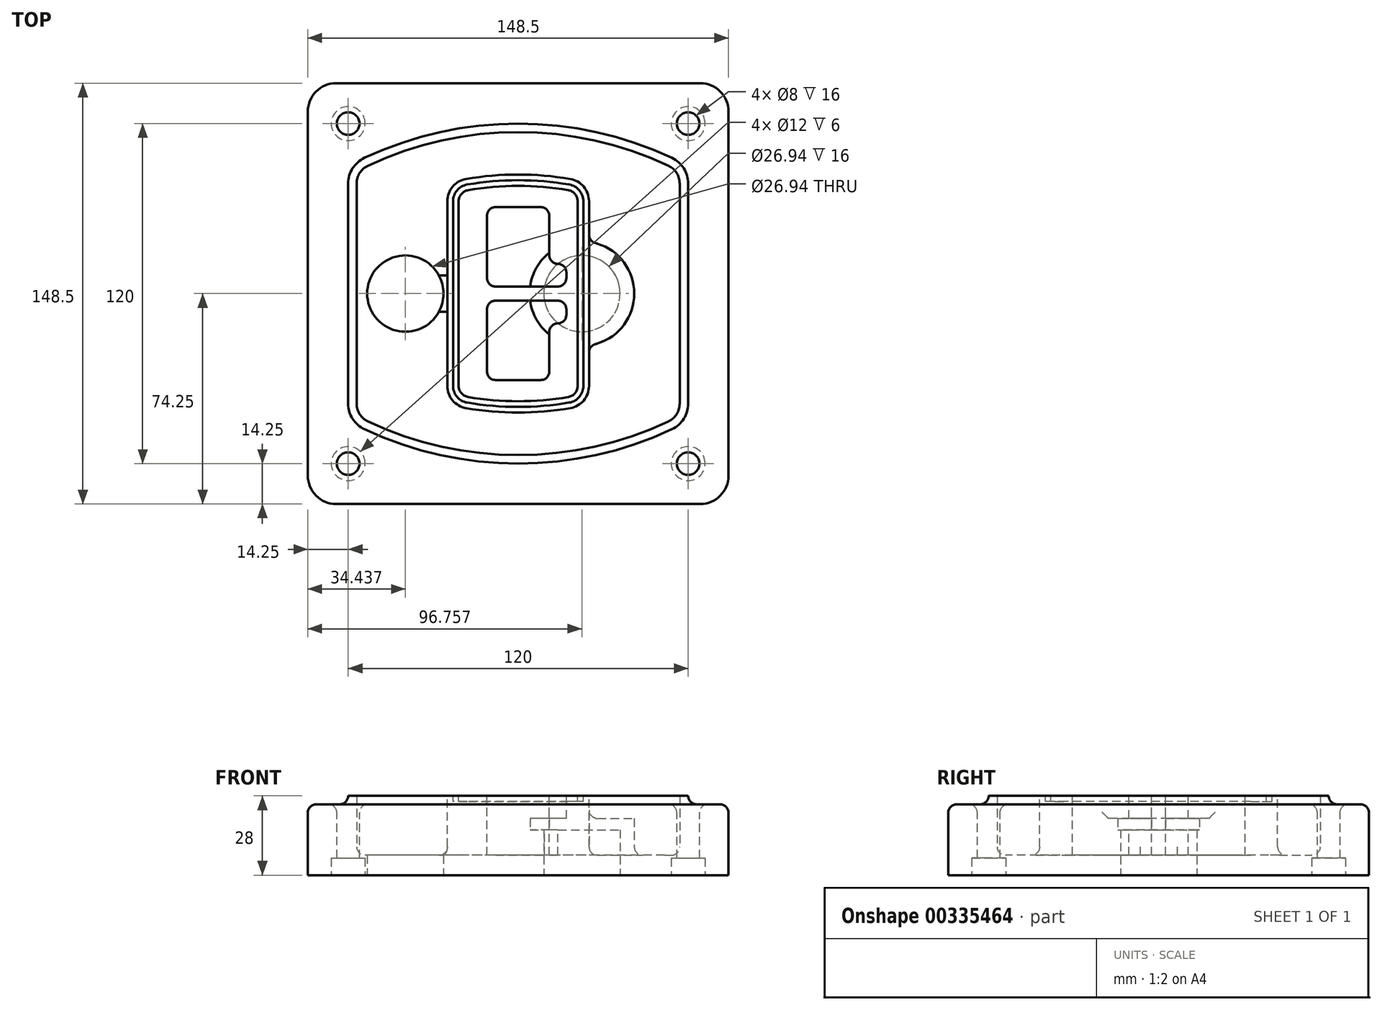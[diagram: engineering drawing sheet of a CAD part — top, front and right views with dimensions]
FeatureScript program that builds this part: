
annotation { "Feature Type Name" : "Feature", "Feature Type Description" : "" }
export const myFeature = defineFeature(function(context is Context, id is Id, definition is map)
    precondition{}
    {
        {
            var Q0;
            Q0=qCreatedBy(makeId("Top.planeOp"),FACE);
            var sketch = newSketch(context, id + "F0", { "sketchPlane" : qUnion([Q0])});
            skPoint(sketch, "E0.rect.middle", {"position": v(0, 0) * mm});
            skLineSegment(sketch, "E1.bottom", {"start": v(-64.25, -74.25) * mm, "end": v(64.25, -74.25) * mm});
            skLineSegment(sketch, "E1.top", {"start": v(-64.25, 74.25) * mm, "end": v(64.25, 74.25) * mm});
            skLineSegment(sketch, "E1.left", {"start": v(-74.25, -64.25) * mm, "end": v(-74.25, 64.25) * mm});
            skLineSegment(sketch, "E1.right", {"start": v(74.25, -64.25) * mm, "end": v(74.25, 64.25) * mm});
            skLineSegment(sketch, "E2", {"start": v(-74.25, 74.25) * mm, "end": v(74.25, -74.25) * mm, "construction": true});
            skLineSegment(sketch, "E3", {"start": v(74.25, 74.25) * mm, "end": v(-74.25, -74.25) * mm, "construction": true});
            skCircle(sketch, "E4", {"center": v(-60, 60) * mm, "radius": 4 * mm});
            skCircle(sketch, "E5", {"center": v(60, 60) * mm, "radius": 4 * mm});
            skCircle(sketch, "E6", {"center": v(60, -60) * mm, "radius": 4 * mm});
            skCircle(sketch, "E7", {"center": v(-60, -60) * mm, "radius": 4 * mm});
            skLineSegment(sketch, "E8", {"start": v(-60, 60) * mm, "end": v(60, 60) * mm, "construction": true});
            skLineSegment(sketch, "E9", {"start": v(60, 60) * mm, "end": v(60, -60) * mm, "construction": true});
            skLineSegment(sketch, "E10", {"start": v(60, -60) * mm, "end": v(-60, -60) * mm, "construction": true});
            skLineSegment(sketch, "E11", {"start": v(-60, -60) * mm, "end": v(-60, 60) * mm, "construction": true});
            skLineSegment(sketch, "E12", {"start": v(-60, 38.83) * mm, "end": v(-60, -38.83) * mm});
            skLineSegment(sketch, "E13", {"start": v(60, 38.83) * mm, "end": v(60, -38.83) * mm});
            skArc(sketch, "E14", {"start": v(54.26, 47.88) * mm, "mid": v(0, 60) * mm, "end": v(-54.26, 47.88) * mm});
            skArc(sketch, "E15", {"start": v(-54.26, -47.88) * mm, "mid": v(0, -60) * mm, "end": v(54.26, -47.88) * mm});
            skLineSegment(sketch, "E16", {"start": v(-60, 0) * mm, "end": v(60, 0) * mm, "construction": true});
            skPoint(sketch, "E17.visualSharp", {"position": v(-60, -45) * mm});
            skArc(sketch, "E17.filletArc", {"start": v(-60, -38.83) * mm, "mid": v(-58.44, -44.2) * mm, "end": v(-54.26, -47.88) * mm});
            skPoint(sketch, "E18.visualSharp", {"position": v(-60, 45) * mm});
            skArc(sketch, "E18.filletArc", {"start": v(-54.26, 47.88) * mm, "mid": v(-58.44, 44.2) * mm, "end": v(-60, 38.83) * mm});
            skPoint(sketch, "E19.visualSharp", {"position": v(60, 45) * mm});
            skArc(sketch, "E19.filletArc", {"start": v(60, 38.83) * mm, "mid": v(58.44, 44.2) * mm, "end": v(54.26, 47.88) * mm});
            skPoint(sketch, "E20.visualSharp", {"position": v(60, -45) * mm});
            skArc(sketch, "E20.filletArc", {"start": v(54.26, -47.88) * mm, "mid": v(58.44, -44.2) * mm, "end": v(60, -38.83) * mm});
            skPoint(sketch, "E21.visualSharp", {"position": v(-74.25, 74.25) * mm});
            skArc(sketch, "E21.filletArc", {"start": v(-64.25, 74.25) * mm, "mid": v(-71.32, 71.32) * mm, "end": v(-74.25, 64.25) * mm});
            skPoint(sketch, "E22.visualSharp", {"position": v(74.25, 74.25) * mm});
            skArc(sketch, "E22.filletArc", {"start": v(74.25, 64.25) * mm, "mid": v(71.32, 71.32) * mm, "end": v(64.25, 74.25) * mm});
            skPoint(sketch, "E23.visualSharp", {"position": v(74.25, -74.25) * mm});
            skArc(sketch, "E23.filletArc", {"start": v(64.25, -74.25) * mm, "mid": v(71.32, -71.32) * mm, "end": v(74.25, -64.25) * mm});
            skPoint(sketch, "E24.visualSharp", {"position": v(-74.25, -74.25) * mm});
            skArc(sketch, "E24.filletArc", {"start": v(-74.25, -64.25) * mm, "mid": v(-71.32, -71.32) * mm, "end": v(-64.25, -74.25) * mm});
            skArc(sketch, "E25.0", {"start": v(57, 38.83) * mm, "mid": v(55.9, 42.58) * mm, "end": v(52.98, 45.17) * mm});
            skLineSegment(sketch, "E25.1", {"start": v(57, 38.83) * mm, "end": v(57, -38.83) * mm});
            skArc(sketch, "E25.2", {"start": v(52.98, -45.17) * mm, "mid": v(55.9, -42.58) * mm, "end": v(57, -38.83) * mm});
            skArc(sketch, "E25.3", {"start": v(-52.98, -45.17) * mm, "mid": v(0, -57) * mm, "end": v(52.98, -45.17) * mm});
            skArc(sketch, "E25.4", {"start": v(-57, -38.83) * mm, "mid": v(-55.9, -42.58) * mm, "end": v(-52.98, -45.17) * mm});
            skArc(sketch, "E25.5", {"start": v(52.98, 45.17) * mm, "mid": v(0, 57) * mm, "end": v(-52.98, 45.17) * mm});
            skLineSegment(sketch, "E25.6", {"start": v(-57, 38.83) * mm, "end": v(-57, -38.83) * mm});
            skArc(sketch, "E25.7", {"start": v(-52.98, 45.17) * mm, "mid": v(-55.9, 42.58) * mm, "end": v(-57, 38.83) * mm});
            skArc(sketch, "E26.0", {"start": v(-55.96, 51.5) * mm, "mid": v(-61.82, 46.33) * mm, "end": v(-64, 38.83) * mm});
            skArc(sketch, "E26.1", {"start": v(55.96, 51.5) * mm, "mid": v(0, 64) * mm, "end": v(-55.96, 51.5) * mm});
            skArc(sketch, "E26.2", {"start": v(64, 38.83) * mm, "mid": v(61.82, 46.33) * mm, "end": v(55.96, 51.5) * mm});
            skLineSegment(sketch, "E26.3", {"start": v(64, 38.83) * mm, "end": v(64, -38.83) * mm});
            skArc(sketch, "E26.4", {"start": v(55.96, -51.5) * mm, "mid": v(61.82, -46.33) * mm, "end": v(64, -38.83) * mm});
            skLineSegment(sketch, "E26.5", {"start": v(-64, 38.83) * mm, "end": v(-64, -38.83) * mm});
            skArc(sketch, "E26.6", {"start": v(-55.96, -51.5) * mm, "mid": v(0, -64) * mm, "end": v(55.96, -51.5) * mm});
            skArc(sketch, "E26.7", {"start": v(-64, -38.83) * mm, "mid": v(-61.82, -46.33) * mm, "end": v(-55.96, -51.5) * mm});
            skSolve(sketch);
        }
        {
            var Q0;
            Q0=makeQuery(id+"F0.imprint","IMPRINT",FACE,{"disambiguationData":[TD([[makeQuery(id+"F0.imprint","IMPRINT",EDGE,{"derivedFrom":sQuery(id+"F0.wireOp",EDGE,"E1.bottom")}),1.0]])]});
            var Q1;
            Q1=makeQuery(id+"F0.imprint","IMPRINT",FACE,{"disambiguationData":[TD([[makeQuery(id+"F0.imprint","IMPRINT",EDGE,{"derivedFrom":sQuery(id+"F0.wireOp",EDGE,"E12")}),1.0]])]});
            var Q2;
            Q2=makeQuery(id+"F0.imprint","IMPRINT",FACE,{"disambiguationData":[TD([[makeQuery(id+"F0.imprint","IMPRINT",EDGE,{"derivedFrom":sQuery(id+"F0.wireOp",EDGE,"E25.0")}),1.0]])]});
            var Q3;
            Q3=makeQuery(id+"F0.imprint","IMPRINT",FACE,{"disambiguationData":[TD([[makeQuery(id+"F0.imprint","IMPRINT",EDGE,{"derivedFrom":sQuery(id+"F0.wireOp",EDGE,"E12")}),-1.0]])]});
            extrude(context, id + "F1", {"entities" : qUnion([Q0, Q1, Q2, Q3]), "oppositeDirection" : true, "depth" : 25 * mm});
        }
        {
            var Q0;
            Q0=makeQuery(id+"F0.imprint","IMPRINT",FACE,{"disambiguationData":[TD([[makeQuery(id+"F0.imprint","IMPRINT",EDGE,{"derivedFrom":sQuery(id+"F0.wireOp",EDGE,"E12")}),1.0]])]});
            extrude(context, id + "F2", {"entities" : qUnion([Q0]), "operationType" : NewBodyOperationType.ADD, "depth" : 3 * mm});
        }
        {
            var Q0;
            Q0=makeQuery(id+"F0.imprint","IMPRINT",FACE,{"disambiguationData":[TD([[makeQuery(id+"F0.imprint","IMPRINT",EDGE,{"derivedFrom":sQuery(id+"F0.wireOp",EDGE,"E25.0")}),1.0]])]});
            extrude(context, id + "F3", {"entities" : qUnion([Q0]), "operationType" : NewBodyOperationType.REMOVE, "oppositeDirection" : true, "depth" : 18 * mm});
        }
        {
            var Q0;
            Q0=makeQuery(id+"F2.opExtrude","CAP_FACE",FACE,{"disambiguationData":[OSD([sQuery(id+"F0.wireOp",EDGE,"E12"),sQuery(id+"F0.wireOp",EDGE,"E13"),sQuery(id+"F0.wireOp",EDGE,"E14"),sQuery(id+"F0.wireOp",EDGE,"E15"),sQuery(id+"F0.wireOp",EDGE,"E17.filletArc"),sQuery(id+"F0.wireOp",EDGE,"E18.filletArc"),sQuery(id+"F0.wireOp",EDGE,"E19.filletArc"),sQuery(id+"F0.wireOp",EDGE,"E20.filletArc"),sQuery(id+"F0.wireOp",EDGE,"E25.0"),sQuery(id+"F0.wireOp",EDGE,"E25.1"),sQuery(id+"F0.wireOp",EDGE,"E25.2"),sQuery(id+"F0.wireOp",EDGE,"E25.3"),sQuery(id+"F0.wireOp",EDGE,"E25.4"),sQuery(id+"F0.wireOp",EDGE,"E25.5"),sQuery(id+"F0.wireOp",EDGE,"E25.6"),sQuery(id+"F0.wireOp",EDGE,"E25.7")])],"isStart":false});
            var sketch = newSketch(context, id + "F4", { "sketchPlane" : qUnion([Q0])});
            skArc(sketch, "E27.0", {"start": v(-18.34, -40.45) * mm, "mid": v(0, -42) * mm, "end": v(18.34, -40.45) * mm});
            skArc(sketch, "E28.0", {"start": v(18.34, 40.45) * mm, "mid": v(0, 42) * mm, "end": v(-18.34, 40.45) * mm});
            skLineSegment(sketch, "E29", {"start": v(-25, 32.57) * mm, "end": v(-25, -32.57) * mm});
            skLineSegment(sketch, "E30", {"start": v(25, 32.57) * mm, "end": v(25, -32.57) * mm});
            skLineSegment(sketch, "E31", {"start": v(-25, 39.1) * mm, "end": v(25, 39.1) * mm, "construction": true});
            skLineSegment(sketch, "E32", {"start": v(-25, -39.1) * mm, "end": v(25, -39.1) * mm, "construction": true});
            skPoint(sketch, "E33.visualSharp", {"position": v(-25, 39.1) * mm});
            skArc(sketch, "E33.filletArc", {"start": v(-18.34, 40.45) * mm, "mid": v(-23.11, 37.73) * mm, "end": v(-25, 32.57) * mm});
            skPoint(sketch, "E34.visualSharp", {"position": v(25, 39.1) * mm});
            skArc(sketch, "E34.filletArc", {"start": v(25, 32.57) * mm, "mid": v(23.11, 37.73) * mm, "end": v(18.34, 40.45) * mm});
            skPoint(sketch, "E35.visualSharp", {"position": v(25, -39.1) * mm});
            skArc(sketch, "E35.filletArc", {"start": v(18.34, -40.45) * mm, "mid": v(23.11, -37.73) * mm, "end": v(25, -32.57) * mm});
            skPoint(sketch, "E36.visualSharp", {"position": v(-25, -39.1) * mm});
            skArc(sketch, "E36.filletArc", {"start": v(-25, -32.57) * mm, "mid": v(-23.11, -37.73) * mm, "end": v(-18.34, -40.45) * mm});
            skArc(sketch, "E37.0", {"start": v(52.98, 45.17) * mm, "mid": v(0, 57) * mm, "end": v(-52.98, 45.17) * mm});
            skArc(sketch, "E37.1", {"start": v(-52.98, 45.17) * mm, "mid": v(-55.9, 42.58) * mm, "end": v(-57, 38.83) * mm});
            skLineSegment(sketch, "E37.2", {"start": v(-57, 38.83) * mm, "end": v(-57, -38.83) * mm});
            skArc(sketch, "E37.3", {"start": v(-57, -38.83) * mm, "mid": v(-55.9, -42.58) * mm, "end": v(-52.98, -45.17) * mm});
            skArc(sketch, "E37.4", {"start": v(-52.98, -45.17) * mm, "mid": v(0, -57) * mm, "end": v(52.98, -45.17) * mm});
            skArc(sketch, "E37.5", {"start": v(52.98, -45.17) * mm, "mid": v(55.9, -42.58) * mm, "end": v(57, -38.83) * mm});
            skLineSegment(sketch, "E37.6", {"start": v(57, 38.83) * mm, "end": v(57, -38.83) * mm});
            skArc(sketch, "E37.7", {"start": v(57, 38.83) * mm, "mid": v(55.9, 42.58) * mm, "end": v(52.98, 45.17) * mm});
            skLineSegment(sketch, "E38.0", {"start": v(23, 32.57) * mm, "end": v(23, -32.57) * mm});
            skArc(sketch, "E38.1", {"start": v(18, -38.48) * mm, "mid": v(21.58, -36.44) * mm, "end": v(23, -32.57) * mm});
            skArc(sketch, "E38.2", {"start": v(-18, -38.48) * mm, "mid": v(0, -40) * mm, "end": v(18, -38.48) * mm});
            skArc(sketch, "E38.3", {"start": v(-23, -32.57) * mm, "mid": v(-21.58, -36.44) * mm, "end": v(-18, -38.48) * mm});
            skLineSegment(sketch, "E38.4", {"start": v(-23, 32.57) * mm, "end": v(-23, -32.57) * mm});
            skArc(sketch, "E38.5", {"start": v(23, 32.57) * mm, "mid": v(21.58, 36.44) * mm, "end": v(18, 38.48) * mm});
            skArc(sketch, "E38.6", {"start": v(-18, 38.48) * mm, "mid": v(-21.58, 36.44) * mm, "end": v(-23, 32.57) * mm});
            skArc(sketch, "E38.7", {"start": v(18, 38.48) * mm, "mid": v(0, 40) * mm, "end": v(-18, 38.48) * mm});
            skArc(sketch, "E39.0", {"start": v(21, 32.57) * mm, "mid": v(20.06, 35.15) * mm, "end": v(17.67, 36.5) * mm});
            skLineSegment(sketch, "E39.1", {"start": v(21, 32.57) * mm, "end": v(21, -32.57) * mm});
            skArc(sketch, "E39.2", {"start": v(17.67, -36.5) * mm, "mid": v(20.06, -35.15) * mm, "end": v(21, -32.57) * mm});
            skArc(sketch, "E39.3", {"start": v(-17.67, -36.5) * mm, "mid": v(0, -38) * mm, "end": v(17.67, -36.5) * mm});
            skArc(sketch, "E39.4", {"start": v(-21, -32.57) * mm, "mid": v(-20.06, -35.15) * mm, "end": v(-17.67, -36.5) * mm});
            skArc(sketch, "E39.5", {"start": v(17.67, 36.5) * mm, "mid": v(0, 38) * mm, "end": v(-17.67, 36.5) * mm});
            skLineSegment(sketch, "E39.6", {"start": v(-21, 32.57) * mm, "end": v(-21, -32.57) * mm});
            skArc(sketch, "E39.7", {"start": v(-17.67, 36.5) * mm, "mid": v(-20.06, 35.15) * mm, "end": v(-21, 32.57) * mm});
            skLineSegment(sketch, "E40", {"start": v(-25, 0) * mm, "end": v(25, 0) * mm, "construction": true});
            skLineSegment(sketch, "E41", {"start": v(-11, 5.5) * mm, "end": v(-11, 27.5) * mm});
            skLineSegment(sketch, "E42", {"start": v(-8, 30.5) * mm, "end": v(8, 30.5) * mm});
            skLineSegment(sketch, "E43", {"start": v(11, 27.5) * mm, "end": v(11, 13.5) * mm});
            skLineSegment(sketch, "E44", {"start": v(14, 10.5) * mm, "end": v(14, 10.5) * mm});
            skLineSegment(sketch, "E45", {"start": v(17, 7.5) * mm, "end": v(17, 5.5) * mm});
            skLineSegment(sketch, "E46", {"start": v(14, 2.5) * mm, "end": v(-8, 2.5) * mm});
            skPoint(sketch, "E47.visualSharp", {"position": v(-11, 30.5) * mm});
            skArc(sketch, "E47.filletArc", {"start": v(-8, 30.5) * mm, "mid": v(-10.12, 29.62) * mm, "end": v(-11, 27.5) * mm});
            skPoint(sketch, "E48.visualSharp", {"position": v(11, 30.5) * mm});
            skArc(sketch, "E48.filletArc", {"start": v(11, 27.5) * mm, "mid": v(10.12, 29.62) * mm, "end": v(8, 30.5) * mm});
            skPoint(sketch, "E49.visualSharp", {"position": v(11, 10.5) * mm});
            skArc(sketch, "E49.filletArc", {"start": v(11, 13.5) * mm, "mid": v(11.88, 11.38) * mm, "end": v(14, 10.5) * mm});
            skPoint(sketch, "E50.visualSharp", {"position": v(17, 10.5) * mm});
            skArc(sketch, "E50.filletArc", {"start": v(17, 7.5) * mm, "mid": v(16.12, 9.62) * mm, "end": v(14, 10.5) * mm});
            skPoint(sketch, "E51.visualSharp", {"position": v(17, 2.5) * mm});
            skArc(sketch, "E51.filletArc", {"start": v(14, 2.5) * mm, "mid": v(16.12, 3.38) * mm, "end": v(17, 5.5) * mm});
            skPoint(sketch, "E52.visualSharp", {"position": v(-11, 2.5) * mm});
            skArc(sketch, "E52.filletArc", {"start": v(-11, 5.5) * mm, "mid": v(-10.12, 3.38) * mm, "end": v(-8, 2.5) * mm});
            skLineSegment(sketch, "E53.0.MirrorCS", {"start": v(14, -2.5) * mm, "end": v(-8, -2.5) * mm});
            skArc(sketch, "E54.0.MirrorCS", {"start": v(-11, -5.5) * mm, "mid": v(-10.12, -3.38) * mm, "end": v(-8, -2.5) * mm});
            skLineSegment(sketch, "E55.0.MirrorCS", {"start": v(-11, -5.5) * mm, "end": v(-11, -27.5) * mm});
            skArc(sketch, "E56.0.MirrorCS", {"start": v(-8, -30.5) * mm, "mid": v(-10.12, -29.62) * mm, "end": v(-11, -27.5) * mm});
            skLineSegment(sketch, "E57.0.MirrorCS", {"start": v(-8, -30.5) * mm, "end": v(8, -30.5) * mm});
            skArc(sketch, "E58.0.MirrorCS", {"start": v(11, -27.5) * mm, "mid": v(10.12, -29.62) * mm, "end": v(8, -30.5) * mm});
            skLineSegment(sketch, "E59.0.MirrorCS", {"start": v(11, -27.5) * mm, "end": v(11, -13.5) * mm});
            skArc(sketch, "E60.0.MirrorCS", {"start": v(11, -13.5) * mm, "mid": v(11.88, -11.38) * mm, "end": v(14, -10.5) * mm});
            skArc(sketch, "E61.0.MirrorCS", {"start": v(17, -7.5) * mm, "mid": v(16.12, -9.62) * mm, "end": v(14, -10.5) * mm});
            skLineSegment(sketch, "E62.0.MirrorCS", {"start": v(17, -7.5) * mm, "end": v(17, -5.5) * mm});
            skArc(sketch, "E63.0.MirrorCS", {"start": v(14, -2.5) * mm, "mid": v(16.12, -3.38) * mm, "end": v(17, -5.5) * mm});
            skSolve(sketch);
        }
        {
            var Q0;
            Q0=makeQuery(id+"F4.imprint","IMPRINT",FACE,{"disambiguationData":[TD([[makeQuery(id+"F4.imprint","IMPRINT",EDGE,{"derivedFrom":sQuery(id+"F4.wireOp",EDGE,"E27.0")}),1.0]])]});
            var Q1;
            Q1=makeQuery(id+"F4.imprint","IMPRINT",FACE,{"disambiguationData":[TD([[makeQuery(id+"F4.imprint","IMPRINT",EDGE,{"derivedFrom":sQuery(id+"F4.wireOp",EDGE,"E38.0")}),-1.0]])]});
            var Q2;
            Q2=makeQuery(id+"F4.imprint","IMPRINT",FACE,{"disambiguationData":[TD([[makeQuery(id+"F4.imprint","IMPRINT",EDGE,{"derivedFrom":sQuery(id+"F4.wireOp",EDGE,"E39.0")}),1.0]])]});
            extrude(context, id + "F5", {"entities" : qUnion([Q0, Q1, Q2]), "operationType" : NewBodyOperationType.ADD, "endBound" : BoundingType.UP_TO_NEXT, "oppositeDirection" : true, "depth" : 25 * mm});
        }
        {
            var Q0;
            Q0=makeQuery(id+"F4.imprint","IMPRINT",FACE,{"disambiguationData":[TD([[makeQuery(id+"F4.imprint","IMPRINT",EDGE,{"derivedFrom":sQuery(id+"F4.wireOp",EDGE,"E38.0")}),-1.0]])]});
            extrude(context, id + "F6", {"entities" : qUnion([Q0]), "operationType" : NewBodyOperationType.REMOVE, "oppositeDirection" : true, "depth" : 2 * mm});
        }
        {
            var Q0;
            Q0=makeQuery(id+"F1.opExtrude","CAP_FACE",FACE,{"disambiguationData":[OSD([sQuery(id+"F0.wireOp",EDGE,"E1.bottom"),sQuery(id+"F0.wireOp",EDGE,"E1.top"),sQuery(id+"F0.wireOp",EDGE,"E1.left"),sQuery(id+"F0.wireOp",EDGE,"E1.right"),sQuery(id+"F0.wireOp",EDGE,"E4"),sQuery(id+"F0.wireOp",EDGE,"E5"),sQuery(id+"F0.wireOp",EDGE,"E6"),sQuery(id+"F0.wireOp",EDGE,"E7"),sQuery(id+"F0.wireOp",EDGE,"E21.filletArc"),sQuery(id+"F0.wireOp",EDGE,"E22.filletArc"),sQuery(id+"F0.wireOp",EDGE,"E23.filletArc"),sQuery(id+"F0.wireOp",EDGE,"E24.filletArc")])],"isStart":false});
            var sketch = newSketch(context, id + "F7", { "sketchPlane" : qUnion([Q0])});
            skCircle(sketch, "E64", {"center": v(22.5, 0) * mm, "radius": 13.47 * mm});
            skCircle(sketch, "E65", {"center": v(-39.81, 0) * mm, "radius": 13.47 * mm});
            skLineSegment(sketch, "E66", {"start": v(74.25, 0) * mm, "end": v(-74.25, 0) * mm});
            skCircle(sketch, "E67", {"center": v(22.5, 0) * mm, "radius": 18.47 * mm});
            skCircle(sketch, "E68", {"center": v(60, -60) * mm, "radius": 6 * mm});
            skCircle(sketch, "E69", {"center": v(-60, -60) * mm, "radius": 6 * mm});
            skCircle(sketch, "E70", {"center": v(-60, 60) * mm, "radius": 6 * mm});
            skCircle(sketch, "E71", {"center": v(60, 60) * mm, "radius": 6 * mm});
            skSolve(sketch);
        }
        {
            var Q0;
            {var subQ1=sQuery(id+"F7.wireOp",EDGE,"E66");var subQ4=sQuery(id+"F7.wireOp",EDGE,"E64");var subQ6=makeQuery(id+"F7.imprint","INTERSECT",VERTEX,{"disambiguationData":[OD(0.0)],"derivedFrom":[subQ4,subQ1]});Q0=makeQuery(id+"F7.imprint","IMPRINT",FACE,{"disambiguationData":[TD([[makeQuery(id+"F7.imprint","IMPRINT",EDGE,{"disambiguationData":[TD([[subQ6,-1.0]])],"derivedFrom":subQ4}),-1.0]])]});}
            var Q1;
            {var subQ0=sQuery(id+"F7.wireOp",EDGE,"E66");var subQ1=sQuery(id+"F7.wireOp",EDGE,"E64");var subQ3=makeQuery(id+"F7.imprint","INTERSECT",VERTEX,{"disambiguationData":[OD(0.0)],"derivedFrom":[subQ1,subQ0]});Q1=makeQuery(id+"F7.imprint","IMPRINT",FACE,{"disambiguationData":[TD([[makeQuery(id+"F7.imprint","IMPRINT",EDGE,{"disambiguationData":[TD([[subQ3,-1.0]])],"derivedFrom":subQ1}),1.0]])]});}
            var Q2;
            {var subQ0=sQuery(id+"F7.wireOp",EDGE,"E66");var subQ1=sQuery(id+"F7.wireOp",EDGE,"E64");var subQ3=makeQuery(id+"F7.imprint","INTERSECT",VERTEX,{"disambiguationData":[OD(0.0)],"derivedFrom":[subQ1,subQ0]});Q2=makeQuery(id+"F7.imprint","IMPRINT",FACE,{"disambiguationData":[TD([[makeQuery(id+"F7.imprint","IMPRINT",EDGE,{"disambiguationData":[TD([[subQ3,1.0]])],"derivedFrom":subQ1}),1.0]])]});}
            var Q3;
            {var subQ1=sQuery(id+"F7.wireOp",EDGE,"E66");var subQ4=sQuery(id+"F7.wireOp",EDGE,"E64");var subQ6=makeQuery(id+"F7.imprint","INTERSECT",VERTEX,{"disambiguationData":[OD(0.0)],"derivedFrom":[subQ4,subQ1]});Q3=makeQuery(id+"F7.imprint","IMPRINT",FACE,{"disambiguationData":[TD([[makeQuery(id+"F7.imprint","IMPRINT",EDGE,{"disambiguationData":[TD([[subQ6,1.0]])],"derivedFrom":subQ4}),-1.0]])]});}
            extrude(context, id + "F8", {"entities" : qUnion([Q0, Q1, Q2, Q3]), "operationType" : NewBodyOperationType.ADD, "oppositeDirection" : true, "depth" : 20 * mm});
        }
        {
            var Q0;
            {var subQ0=sQuery(id+"F7.wireOp",EDGE,"E66");var subQ1=sQuery(id+"F7.wireOp",EDGE,"E64");var subQ3=makeQuery(id+"F7.imprint","INTERSECT",VERTEX,{"disambiguationData":[OD(0.0)],"derivedFrom":[subQ1,subQ0]});Q0=makeQuery(id+"F7.imprint","IMPRINT",FACE,{"disambiguationData":[TD([[makeQuery(id+"F7.imprint","IMPRINT",EDGE,{"disambiguationData":[TD([[subQ3,-1.0]])],"derivedFrom":subQ1}),1.0]])]});}
            var Q1;
            {var subQ0=sQuery(id+"F7.wireOp",EDGE,"E66");var subQ1=sQuery(id+"F7.wireOp",EDGE,"E64");var subQ3=makeQuery(id+"F7.imprint","INTERSECT",VERTEX,{"disambiguationData":[OD(0.0)],"derivedFrom":[subQ1,subQ0]});Q1=makeQuery(id+"F7.imprint","IMPRINT",FACE,{"disambiguationData":[TD([[makeQuery(id+"F7.imprint","IMPRINT",EDGE,{"disambiguationData":[TD([[subQ3,1.0]])],"derivedFrom":subQ1}),1.0]])]});}
            extrude(context, id + "F9", {"entities" : qUnion([Q0, Q1]), "operationType" : NewBodyOperationType.REMOVE, "oppositeDirection" : true, "depth" : 16 * mm});
        }
        {
            var Q0;
            {var subQ0=sQuery(id+"F7.wireOp",EDGE,"E66");var subQ1=sQuery(id+"F7.wireOp",EDGE,"E65");var subQ3=makeQuery(id+"F7.imprint","INTERSECT",VERTEX,{"disambiguationData":[OD(0.0)],"derivedFrom":[subQ1,subQ0]});Q0=makeQuery(id+"F7.imprint","IMPRINT",FACE,{"disambiguationData":[TD([[makeQuery(id+"F7.imprint","IMPRINT",EDGE,{"disambiguationData":[TD([[subQ3,-1.0]])],"derivedFrom":subQ1}),1.0]])]});}
            var Q1;
            {var subQ0=sQuery(id+"F7.wireOp",EDGE,"E66");var subQ1=sQuery(id+"F7.wireOp",EDGE,"E65");var subQ3=makeQuery(id+"F7.imprint","INTERSECT",VERTEX,{"disambiguationData":[OD(0.0)],"derivedFrom":[subQ1,subQ0]});Q1=makeQuery(id+"F7.imprint","IMPRINT",FACE,{"disambiguationData":[TD([[makeQuery(id+"F7.imprint","IMPRINT",EDGE,{"disambiguationData":[TD([[subQ3,1.0]])],"derivedFrom":subQ1}),1.0]])]});}
            extrude(context, id + "F10", {"entities" : qUnion([Q0, Q1]), "operationType" : NewBodyOperationType.REMOVE, "oppositeDirection" : true, "depth" : 25 * mm});
        }
        {
            var Q0;
            Q0=makeQuery(id+"F7.imprint","IMPRINT",FACE,{"disambiguationData":[TD([[makeQuery(id+"F7.imprint","IMPRINT",EDGE,{"derivedFrom":sQuery(id+"F7.wireOp",EDGE,"E68")}),1.0]])]});
            var Q1;
            Q1=makeQuery(id+"F7.imprint","IMPRINT",FACE,{"disambiguationData":[TD([[makeQuery(id+"F7.imprint","IMPRINT",EDGE,{"derivedFrom":makeQuery(id+"F1.opExtrude","CAP_EDGE",EDGE,{"disambiguationData":[OSD([sQuery(id+"F0.wireOp",EDGE,"E5")])],"isStart":false})}),-1.0]])]});
            var Q2;
            Q2=makeQuery(id+"F7.imprint","IMPRINT",FACE,{"disambiguationData":[TD([[makeQuery(id+"F7.imprint","IMPRINT",EDGE,{"derivedFrom":sQuery(id+"F7.wireOp",EDGE,"E69")}),1.0]])]});
            var Q3;
            Q3=makeQuery(id+"F7.imprint","IMPRINT",FACE,{"disambiguationData":[TD([[makeQuery(id+"F7.imprint","IMPRINT",EDGE,{"derivedFrom":makeQuery(id+"F1.opExtrude","CAP_EDGE",EDGE,{"disambiguationData":[OSD([sQuery(id+"F0.wireOp",EDGE,"E4")])],"isStart":false})}),-1.0]])]});
            var Q4;
            Q4=makeQuery(id+"F7.imprint","IMPRINT",FACE,{"disambiguationData":[TD([[makeQuery(id+"F7.imprint","IMPRINT",EDGE,{"derivedFrom":sQuery(id+"F7.wireOp",EDGE,"E70")}),1.0]])]});
            var Q5;
            Q5=makeQuery(id+"F7.imprint","IMPRINT",FACE,{"disambiguationData":[TD([[makeQuery(id+"F7.imprint","IMPRINT",EDGE,{"derivedFrom":makeQuery(id+"F1.opExtrude","CAP_EDGE",EDGE,{"disambiguationData":[OSD([sQuery(id+"F0.wireOp",EDGE,"E7")])],"isStart":false})}),-1.0]])]});
            var Q6;
            Q6=makeQuery(id+"F7.imprint","IMPRINT",FACE,{"disambiguationData":[TD([[makeQuery(id+"F7.imprint","IMPRINT",EDGE,{"derivedFrom":sQuery(id+"F7.wireOp",EDGE,"E71")}),1.0]])]});
            var Q7;
            Q7=makeQuery(id+"F7.imprint","IMPRINT",FACE,{"disambiguationData":[TD([[makeQuery(id+"F7.imprint","IMPRINT",EDGE,{"derivedFrom":makeQuery(id+"F1.opExtrude","CAP_EDGE",EDGE,{"disambiguationData":[OSD([sQuery(id+"F0.wireOp",EDGE,"E6")])],"isStart":false})}),-1.0]])]});
            extrude(context, id + "F11", {"entities" : qUnion([Q0, Q1, Q2, Q3, Q4, Q5, Q6, Q7]), "operationType" : NewBodyOperationType.REMOVE, "oppositeDirection" : true, "depth" : 6 * mm});
        }
        {
            var Q0;
            Q0=makeQuery(id+"F9.boolean.opBoolean","COPY",FACE,{"derivedFrom":makeQuery(id+"F9.opExtrude","CAP_FACE",FACE,{"disambiguationData":[OSD([sQuery(id+"F7.wireOp",EDGE,"E64")])],"isStart":false})});
            var sketch = newSketch(context, id + "F12", { "sketchPlane" : qUnion([Q0])});
            skArc(sketch, "E72.0", {"start": v(11, 14.45) * mm, "mid": v(6.45, 9.13) * mm, "end": v(4.2, 2.5) * mm});
            skArc(sketch, "E72.1", {"start": v(4.2, -2.5) * mm, "mid": v(6.45, -9.13) * mm, "end": v(11, -14.45) * mm});
            skLineSegment(sketch, "E73", {"start": v(4.2, -2.5) * mm, "end": v(14, -2.5) * mm});
            skLineSegment(sketch, "E74.0", {"start": v(14, 2.5) * mm, "end": v(4.2, 2.5) * mm});
            skArc(sketch, "E74.1", {"start": v(14, 2.5) * mm, "mid": v(16.12, 3.38) * mm, "end": v(17, 5.5) * mm});
            skLineSegment(sketch, "E74.2", {"start": v(17, 7.5) * mm, "end": v(17, 5.5) * mm});
            skArc(sketch, "E74.3", {"start": v(17, 7.5) * mm, "mid": v(16.12, 9.62) * mm, "end": v(14, 10.5) * mm});
            skArc(sketch, "E74.4", {"start": v(11, 13.5) * mm, "mid": v(11.88, 11.38) * mm, "end": v(14, 10.5) * mm});
            skLineSegment(sketch, "E74.5", {"start": v(11, 14.45) * mm, "end": v(11, 13.5) * mm});
            skLineSegment(sketch, "E74.7", {"start": v(14, -2.5) * mm, "end": v(4.2, -2.5) * mm});
            skArc(sketch, "E74.8", {"start": v(14, -2.5) * mm, "mid": v(16.12, -3.38) * mm, "end": v(17, -5.5) * mm});
            skLineSegment(sketch, "E74.9", {"start": v(17, -7.5) * mm, "end": v(17, -5.5) * mm});
            skArc(sketch, "E74.10", {"start": v(17, -7.5) * mm, "mid": v(16.12, -9.62) * mm, "end": v(14, -10.5) * mm});
            skArc(sketch, "E74.11", {"start": v(11, -13.5) * mm, "mid": v(11.88, -11.38) * mm, "end": v(14, -10.5) * mm});
            skLineSegment(sketch, "E74.12", {"start": v(11, -14.45) * mm, "end": v(11, -13.5) * mm});
            skPoint(sketch, "E75.orphan", {"position": v(11, -27.5) * mm});
            skPoint(sketch, "E76.orphan", {"position": v(-8, -2.5) * mm});
            skPoint(sketch, "E77.orphan", {"position": v(-8, 2.5) * mm});
            skPoint(sketch, "E78.orphan", {"position": v(11, 27.5) * mm});
            skSolve(sketch);
        }
        {
            var Q0;
            {var subQ7=sQuery(id+"F12.wireOp",EDGE,"E72.0");var subQ14=sQuery(id+"F12.wireOp",EDGE,"E72.1");var subQ16=sQuery(id+"F12.wireOp",EDGE,"E74.1");var subQ18=sQuery(id+"F12.wireOp",EDGE,"E74.8");Q0=qUnion([makeQuery(id+"F12.imprint","IMPRINT",FACE,{"disambiguationData":[TD([[makeQuery(id+"F12.imprint","IMPRINT",EDGE,{"derivedFrom":subQ7}),1.0]])]}),makeQuery(id+"F12.imprint","IMPRINT",FACE,{"disambiguationData":[TD([[makeQuery(id+"F12.imprint","IMPRINT",EDGE,{"derivedFrom":subQ14}),1.0]])]}),makeQuery(id+"F12.imprint","IMPRINT",FACE,{"disambiguationData":[TD([[makeQuery(id+"F12.imprint","IMPRINT",EDGE,{"derivedFrom":subQ16}),1.0]])]}),makeQuery(id+"F12.imprint","IMPRINT",FACE,{"disambiguationData":[TD([[makeQuery(id+"F12.imprint","IMPRINT",EDGE,{"derivedFrom":subQ18}),-1.0]])]})]);}
            var Q1;
            Q1=makeQuery(id+"F5.boolean.opBoolean","SPLIT",FACE,{"disambiguationData":[TD([makeQuery(id+"F5.opExtrude","SWEPT_FACE",FACE,{"disambiguationData":[OSD([sQuery(id+"F4.wireOp",EDGE,"E41")])]})])],"derivedFrom":makeQuery(id+"F3.boolean.opBoolean","COPY",FACE,{"derivedFrom":makeQuery(id+"F3.opExtrude","CAP_FACE",FACE,{"disambiguationData":[OSD([sQuery(id+"F0.wireOp",EDGE,"E25.0"),sQuery(id+"F0.wireOp",EDGE,"E25.1"),sQuery(id+"F0.wireOp",EDGE,"E25.2"),sQuery(id+"F0.wireOp",EDGE,"E25.3"),sQuery(id+"F0.wireOp",EDGE,"E25.4"),sQuery(id+"F0.wireOp",EDGE,"E25.5"),sQuery(id+"F0.wireOp",EDGE,"E25.6"),sQuery(id+"F0.wireOp",EDGE,"E25.7")])],"isStart":false})})});
            extrude(context, id + "F13", {"entities" : qUnion([Q0]), "operationType" : NewBodyOperationType.REMOVE, "endBound" : BoundingType.UP_TO_SURFACE, "endBoundEntityFace" : qUnion([Q1]), "depth" : 25 * mm});
        }
        {
            var Q0;
            Q0=makeQuery(id+"F3.boolean.opBoolean","COPY",EDGE,{"derivedFrom":makeQuery(id+"F3.opExtrude","CAP_EDGE",EDGE,{"disambiguationData":[OSD([sQuery(id+"F0.wireOp",EDGE,"E25.6")])],"isStart":false})});
            var Q1;
            Q1=makeQuery(id+"F8.boolean.opBoolean","INTERSECT",EDGE,{"derivedFrom":[makeQuery(id+"F5.opExtrude","SWEPT_FACE",FACE,{"disambiguationData":[OSD([sQuery(id+"F4.wireOp",EDGE,"E30")])]}),makeQuery(id+"F8.opExtrude","CAP_FACE",FACE,{"disambiguationData":[OSD([sQuery(id+"F7.wireOp",EDGE,"E67")])],"isStart":false})]});
            var Q2;
            Q2=makeQuery(id+"F8.boolean.opBoolean","INTERSECT",EDGE,{"disambiguationData":[OD(1.0)],"derivedFrom":[makeQuery(id+"F5.opExtrude","SWEPT_FACE",FACE,{"disambiguationData":[OSD([sQuery(id+"F4.wireOp",EDGE,"E30")])]}),makeQuery(id+"F8.opExtrude","SWEPT_FACE",FACE,{"disambiguationData":[OSD([sQuery(id+"F7.wireOp",EDGE,"E67")])]})]});
            var Q3;
            {var subQ0=sQuery(id+"F4.wireOp",EDGE,"E30");Q3=makeQuery(id+"F8.boolean.opBoolean","SPLIT",EDGE,{"disambiguationData":[TD([makeQuery(id+"F5.opExtrude","SWEPT_FACE",FACE,{"disambiguationData":[OSD([sQuery(id+"F4.wireOp",EDGE,"E35.filletArc")])]})])],"derivedFrom":makeQuery(id+"F5.opExtrude","CAP_EDGE",EDGE,{"disambiguationData":[OSD([subQ0])],"isStart":false})});}
            var Q4;
            {var subQ0=sQuery(id+"F0.wireOp",EDGE,"E25.7");var subQ1=sQuery(id+"F0.wireOp",EDGE,"E25.1");var subQ2=sQuery(id+"F0.wireOp",EDGE,"E25.6");var subQ3=sQuery(id+"F0.wireOp",EDGE,"E25.5");var subQ4=sQuery(id+"F0.wireOp",EDGE,"E25.4");var subQ5=sQuery(id+"F0.wireOp",EDGE,"E25.0");var subQ6=sQuery(id+"F0.wireOp",EDGE,"E25.2");var subQ7=sQuery(id+"F0.wireOp",EDGE,"E25.3");Q4=makeQuery(id+"F8.boolean.opBoolean","INTERSECT",EDGE,{"derivedFrom":[makeQuery(id+"F5.boolean.opBoolean","SPLIT",FACE,{"disambiguationData":[TD([makeQuery(id+"F2.opExtrude","SWEPT_FACE",FACE,{"disambiguationData":[OSD([subQ5])]})])],"derivedFrom":makeQuery(id+"F3.boolean.opBoolean","COPY",FACE,{"derivedFrom":makeQuery(id+"F3.opExtrude","CAP_FACE",FACE,{"disambiguationData":[OSD([subQ5,subQ1,subQ6,subQ7,subQ4,subQ3,subQ2,subQ0])],"isStart":false})})}),makeQuery(id+"F8.opExtrude","SWEPT_FACE",FACE,{"disambiguationData":[OSD([sQuery(id+"F7.wireOp",EDGE,"E67")])]})]});}
            var Q5;
            Q5=makeQuery(id+"F8.boolean.opBoolean","INTERSECT",EDGE,{"disambiguationData":[OD(0.0)],"derivedFrom":[makeQuery(id+"F5.opExtrude","SWEPT_FACE",FACE,{"disambiguationData":[OSD([sQuery(id+"F4.wireOp",EDGE,"E30")])]}),makeQuery(id+"F8.opExtrude","SWEPT_FACE",FACE,{"disambiguationData":[OSD([sQuery(id+"F7.wireOp",EDGE,"E67")])]})]});
            var Q6;
            {var subQ0=sQuery(id+"F0.wireOp",EDGE,"E21.filletArc");var subQ1=sQuery(id+"F0.wireOp",EDGE,"E7");var subQ2=sQuery(id+"F0.wireOp",EDGE,"E6");var subQ3=sQuery(id+"F0.wireOp",EDGE,"E5");var subQ4=sQuery(id+"F0.wireOp",EDGE,"E4");var subQ5=sQuery(id+"F0.wireOp",EDGE,"E22.filletArc");var subQ6=sQuery(id+"F0.wireOp",EDGE,"E1.bottom");var subQ7=sQuery(id+"F0.wireOp",EDGE,"E1.right");var subQ8=sQuery(id+"F0.wireOp",EDGE,"E1.top");var subQ9=sQuery(id+"F0.wireOp",EDGE,"E1.left");var subQ10=sQuery(id+"F0.wireOp",EDGE,"E23.filletArc");var subQ11=sQuery(id+"F0.wireOp",EDGE,"E24.filletArc");Q6=makeQuery(id+"F2.boolean.opBoolean","SPLIT",FACE,{"disambiguationData":[TD([makeQuery(id+"F1.opExtrude","SWEPT_FACE",FACE,{"disambiguationData":[OSD([subQ6])]})])],"derivedFrom":makeQuery(id+"F1.opExtrude","CAP_FACE",FACE,{"disambiguationData":[OSD([subQ6,subQ8,subQ9,subQ7,subQ4,subQ3,subQ2,subQ1,subQ0,subQ5,subQ10,subQ11])],"isStart":true})});}
            fillet(context, id + "F14", {"entities" : qUnion([Q0, Q1, Q2, Q3, Q4, Q5, Q6]), "radius" : 3 * mm, "tangentPropagation" : true, "allowEdgeOverflow" : false});
        }
    });
